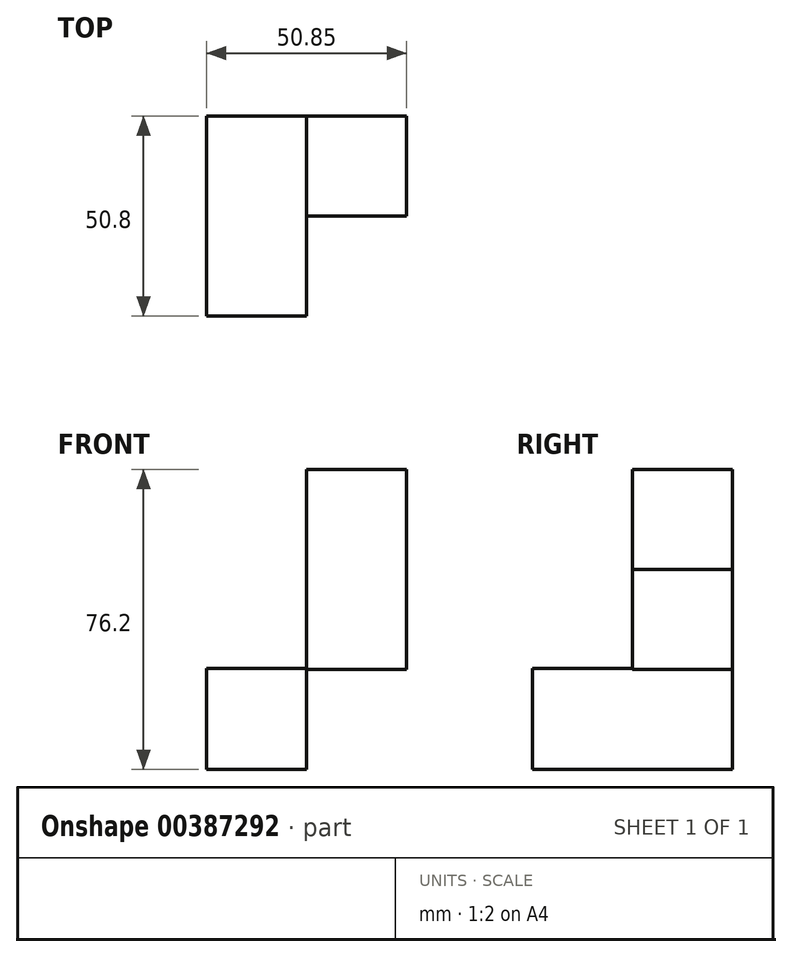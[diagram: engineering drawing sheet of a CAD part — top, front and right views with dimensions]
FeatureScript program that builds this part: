
annotation { "Feature Type Name" : "Feature", "Feature Type Description" : "" }
export const myFeature = defineFeature(function(context is Context, id is Id, definition is map)
    precondition{}
    {
        {
            var Q0;
            Q0=qCreatedBy(makeId("Front.planeOp"),FACE);
            var sketch = newSketch(context, id + "F0", { "sketchPlane" : qUnion([Q0])});
            skLineSegment(sketch, "E0.bottom", {"start": v(0, 0) * mm, "end": v(25.4, 0) * mm});
            skLineSegment(sketch, "E0.top", {"start": v(0, 25.4) * mm, "end": v(25.4, 25.4) * mm});
            skLineSegment(sketch, "E0.left", {"start": v(0, 0) * mm, "end": v(0, 25.4) * mm});
            skLineSegment(sketch, "E0.right", {"start": v(25.4, 0) * mm, "end": v(25.4, 25.4) * mm});
            skLineSegment(sketch, "E1.bottom", {"start": v(0, 0) * mm, "end": v(25.45, 0) * mm});
            skLineSegment(sketch, "E1.top", {"start": v(0, -25.4) * mm, "end": v(25.45, -25.4) * mm});
            skLineSegment(sketch, "E1.left", {"start": v(0, 0) * mm, "end": v(0, -25.4) * mm});
            skLineSegment(sketch, "E1.right", {"start": v(25.45, 0) * mm, "end": v(25.45, -25.4) * mm});
            skLineSegment(sketch, "E2.bottom", {"start": v(0, -25.4) * mm, "end": v(25.4, -25.4) * mm});
            skLineSegment(sketch, "E2.top", {"start": v(0, -50.8) * mm, "end": v(25.4, -50.8) * mm});
            skLineSegment(sketch, "E2.left", {"start": v(0, -25.4) * mm, "end": v(0, -50.8) * mm});
            skLineSegment(sketch, "E2.right", {"start": v(25.4, -25.4) * mm, "end": v(25.4, -50.8) * mm});
            skLineSegment(sketch, "E3.bottom", {"start": v(0, -50.8) * mm, "end": v(-25.4, -50.8) * mm});
            skLineSegment(sketch, "E3.top", {"start": v(0, -25.14) * mm, "end": v(-25.4, -25.14) * mm});
            skLineSegment(sketch, "E3.left", {"start": v(0, -50.8) * mm, "end": v(0, -25.14) * mm});
            skLineSegment(sketch, "E3.right", {"start": v(-25.4, -50.8) * mm, "end": v(-25.4, -25.14) * mm});
            skSolve(sketch);
        }
        {
            var Q0;
            {var subQ0=sQuery(id+"F0.wireOp",EDGE,"E2.bottom");Q0=makeQuery(id+"F0.imprint","IMPRINT",FACE,{"disambiguationData":[TD([[makeQuery(id+"F0.imprint","IMPRINT",EDGE,{"derivedFrom":subQ0}),-1.0]])]});}
            var Q1;
            {var subQ3=sQuery(id+"F0.wireOp",EDGE,"E3.bottom");Q1=makeQuery(id+"F0.imprint","IMPRINT",FACE,{"disambiguationData":[TD([[makeQuery(id+"F0.imprint","IMPRINT",EDGE,{"derivedFrom":subQ3}),-1.0]])]});}
            extrude(context, id + "F1", {"entities" : qUnion([Q0, Q1]), "depth" : 50.8 * mm});
        }
        {
            var Q0;
            Q0=makeQuery(id+"F0.imprint","IMPRINT",FACE,{"disambiguationData":[TD([[makeQuery(id+"F0.imprint","IMPRINT",EDGE,{"derivedFrom":sQuery(id+"F0.wireOp",EDGE,"E0.top")}),-1.0]])]});
            var Q1;
            Q1=makeQuery(id+"F0.imprint","IMPRINT",FACE,{"disambiguationData":[TD([[makeQuery(id+"F0.imprint","IMPRINT",EDGE,{"derivedFrom":sQuery(id+"F0.wireOp",EDGE,"E1.top")}),1.0]])]});
            extrude(context, id + "F2", {"entities" : qUnion([Q0, Q1]), "operationType" : NewBodyOperationType.ADD, "depth" : 25.4 * mm});
        }
    });
